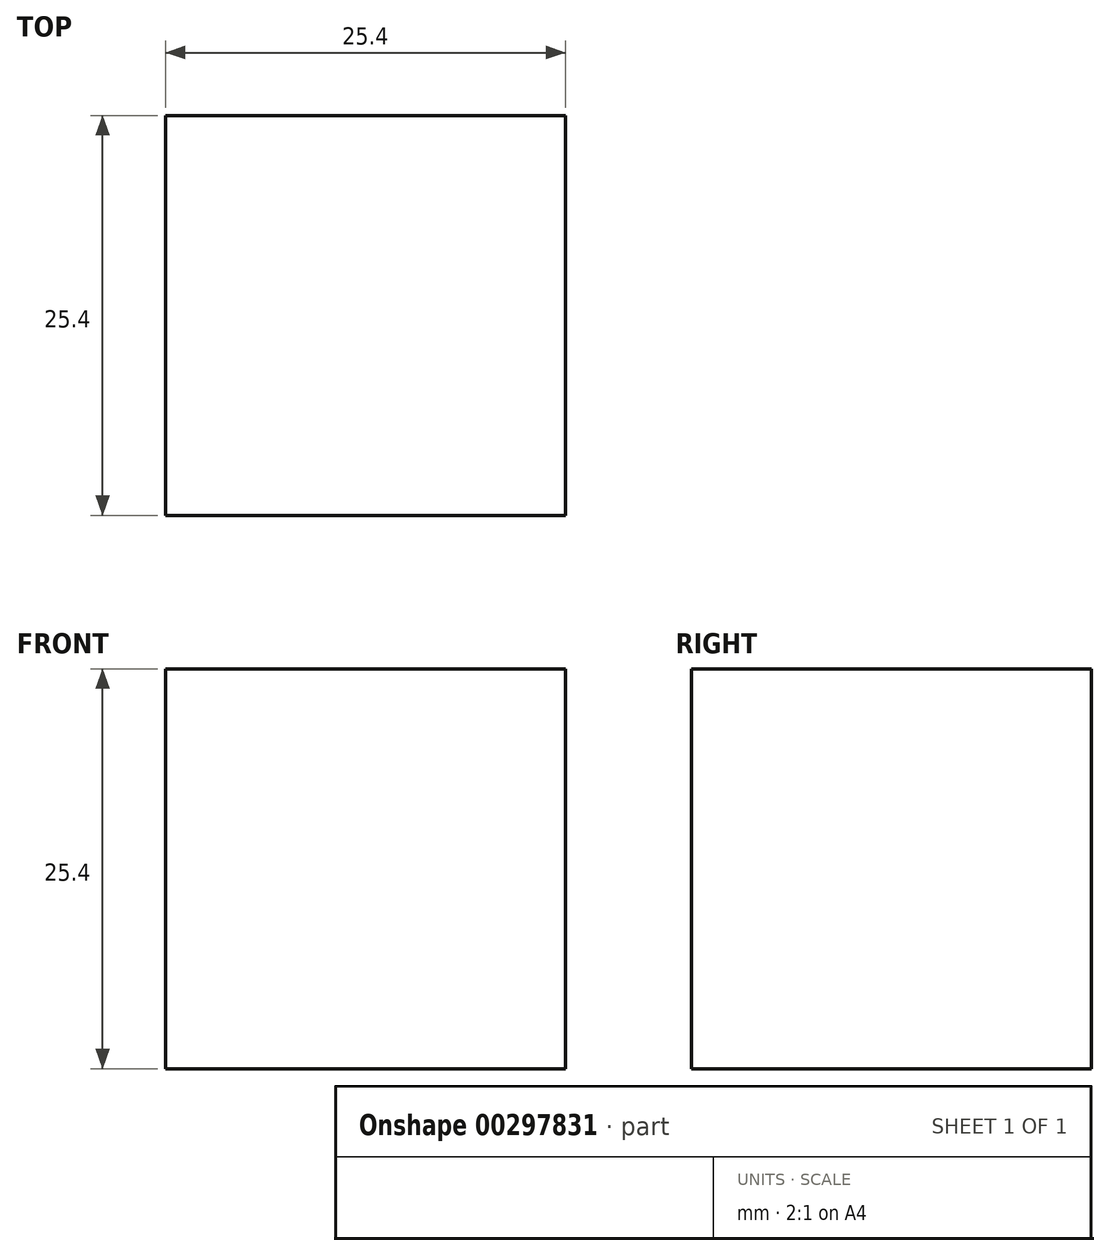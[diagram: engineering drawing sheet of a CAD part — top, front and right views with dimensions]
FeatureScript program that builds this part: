
annotation { "Feature Type Name" : "Feature", "Feature Type Description" : "" }
export const myFeature = defineFeature(function(context is Context, id is Id, definition is map)
    precondition{}
    {
        {
            var Q0;
            Q0=qCreatedBy(makeId("Front.planeOp"),FACE);
            var sketch = newSketch(context, id + "F0", { "sketchPlane" : qUnion([Q0])});
            skLineSegment(sketch, "E0.bottom", {"start": v(12.7, 12.7) * mm, "end": v(-12.7, 12.7) * mm});
            skLineSegment(sketch, "E0.top", {"start": v(12.7, -12.7) * mm, "end": v(-12.7, -12.7) * mm});
            skLineSegment(sketch, "E0.left", {"start": v(12.7, 12.7) * mm, "end": v(12.7, -12.7) * mm});
            skLineSegment(sketch, "E0.right", {"start": v(-12.7, 12.7) * mm, "end": v(-12.7, -12.7) * mm});
            skPoint(sketch, "E0.middle", {"position": v(0, 0) * mm});
            skSolve(sketch);
        }
        {
            var Q0;
            Q0=makeQuery(id+"F0.imprint","IMPRINT",FACE,{"disambiguationData":[TD([[makeQuery(id+"F0.imprint","IMPRINT",EDGE,{"derivedFrom":sQuery(id+"F0.wireOp",EDGE,"E0.bottom")}),1.0]])]});
            extrude(context, id + "F1", {"entities" : qUnion([Q0]), "depth" : 25.4 * mm});
        }
    });
